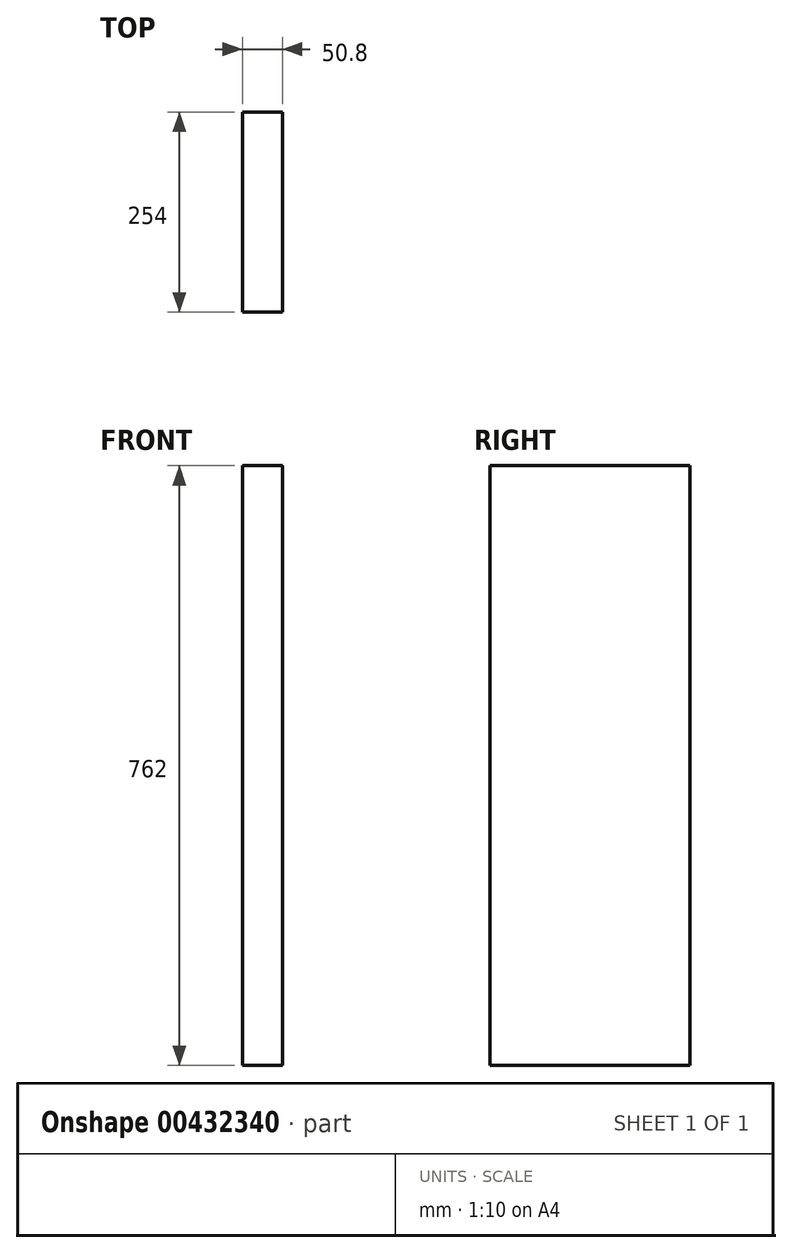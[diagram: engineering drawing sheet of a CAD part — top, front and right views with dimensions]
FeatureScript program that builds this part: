
annotation { "Feature Type Name" : "Feature", "Feature Type Description" : "" }
export const myFeature = defineFeature(function(context is Context, id is Id, definition is map)
    precondition{}
    {
        {
            var Q0;
            Q0=qCreatedBy(makeId("Front.planeOp"),FACE);
            var sketch = newSketch(context, id + "F0", { "sketchPlane" : qUnion([Q0])});
            skLineSegment(sketch, "E0.bottom", {"start": v(0, 0) * mm, "end": v(50.8, 0) * mm});
            skLineSegment(sketch, "E0.top", {"start": v(0, 762) * mm, "end": v(50.8, 762) * mm});
            skLineSegment(sketch, "E0.left", {"start": v(0, 0) * mm, "end": v(0, 762) * mm});
            skLineSegment(sketch, "E0.right", {"start": v(50.8, 0) * mm, "end": v(50.8, 762) * mm});
            skSolve(sketch);
        }
        {
            var Q0;
            Q0=makeQuery(id+"F0.imprint","IMPRINT",FACE,{"disambiguationData":[TD([[makeQuery(id+"F0.imprint","IMPRINT",EDGE,{"derivedFrom":sQuery(id+"F0.wireOp",EDGE,"E0.bottom")}),1.0]])]});
            extrude(context, id + "F1", {"entities" : qUnion([Q0]), "depth" : 254 * mm});
        }
    });
